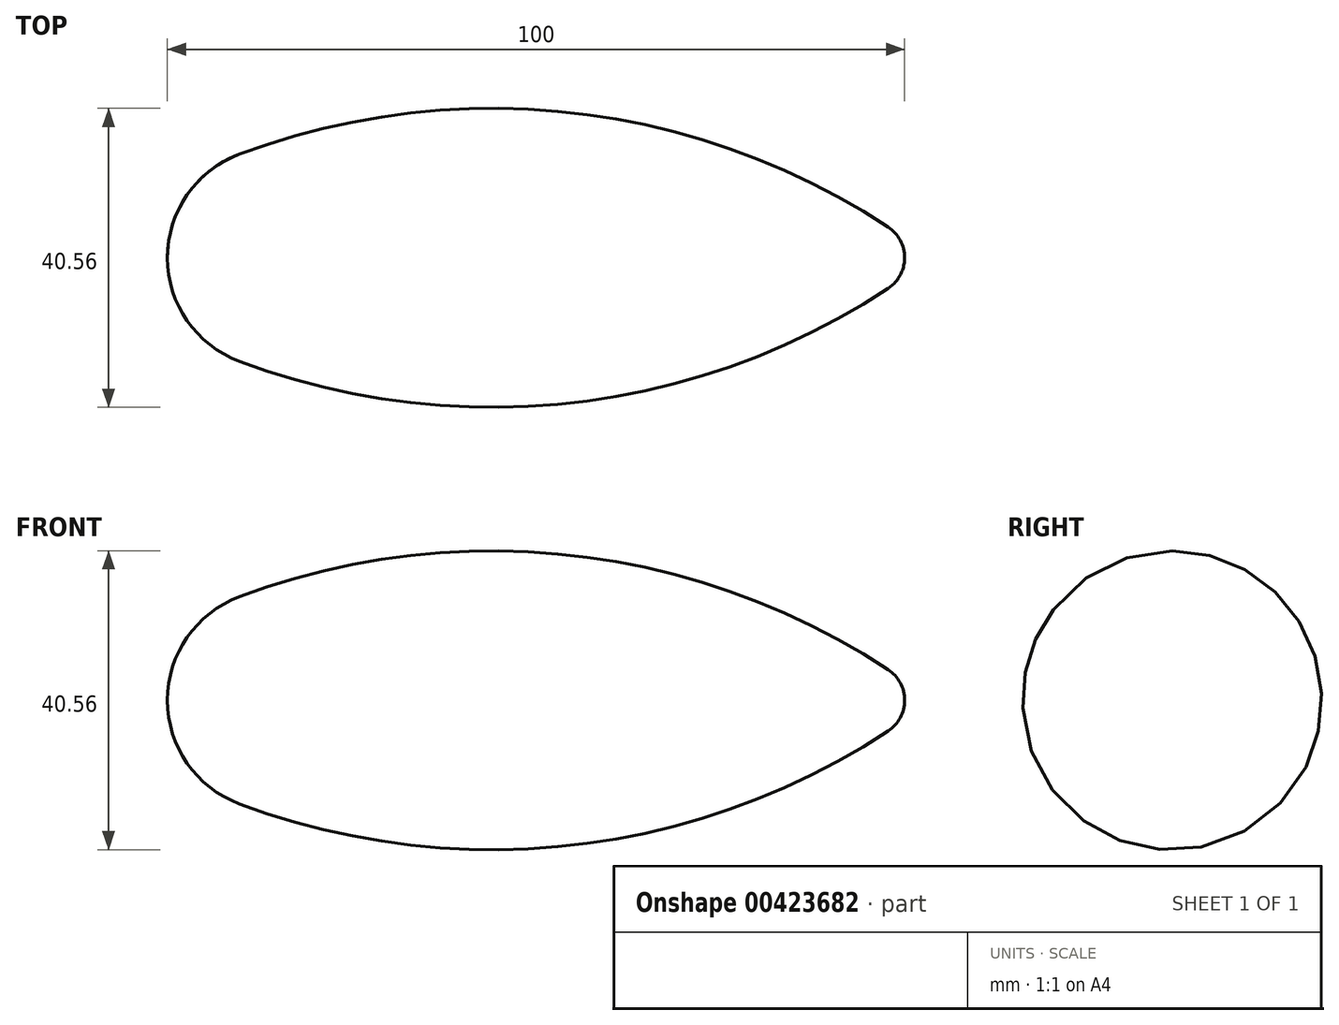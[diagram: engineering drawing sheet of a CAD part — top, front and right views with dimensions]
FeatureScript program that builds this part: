
annotation { "Feature Type Name" : "Feature", "Feature Type Description" : "" }
export const myFeature = defineFeature(function(context is Context, id is Id, definition is map)
    precondition{}
    {
        {
            var Q0;
            Q0=qCreatedBy(makeId("Top.planeOp"),FACE);
            var sketch = newSketch(context, id + "F0", { "sketchPlane" : qUnion([Q0])});
            skArc(sketch, "E0", {"start": v(15, 0) * mm, "mid": v(0, 15) * mm, "end": v(-15, 0) * mm});
            skArc(sketch, "E1", {"start": v(85, 0) * mm, "mid": v(80, 5) * mm, "end": v(75, 0) * mm});
            skLineSegment(sketch, "E2", {"start": v(0, 0) * mm, "end": v(80, 0) * mm});
            skLineSegment(sketch, "E3", {"start": v(50, 0) * mm, "end": v(50, 18) * mm});
            skArc(sketch, "E4", {"start": v(82.75, 4.18) * mm, "mid": v(39.92, 19.67) * mm, "end": v(-5.27, 14.04) * mm});
            skLineSegment(sketch, "E5", {"start": v(-15, 0) * mm, "end": v(85, 0) * mm});
            skSolve(sketch);
        }
        {
            var Q0;
            Q0 = qSketchRegion(id + "F0", true);
            var Q1;
            Q1=sQuery(id+"F0.wireOp",EDGE,"E5");
            revolve(context, id + "F1", {"entities" : qUnion([Q0]), "axis" : qUnion([Q1]), "revolveType" : RevolveType.FULL});
        }
    });
